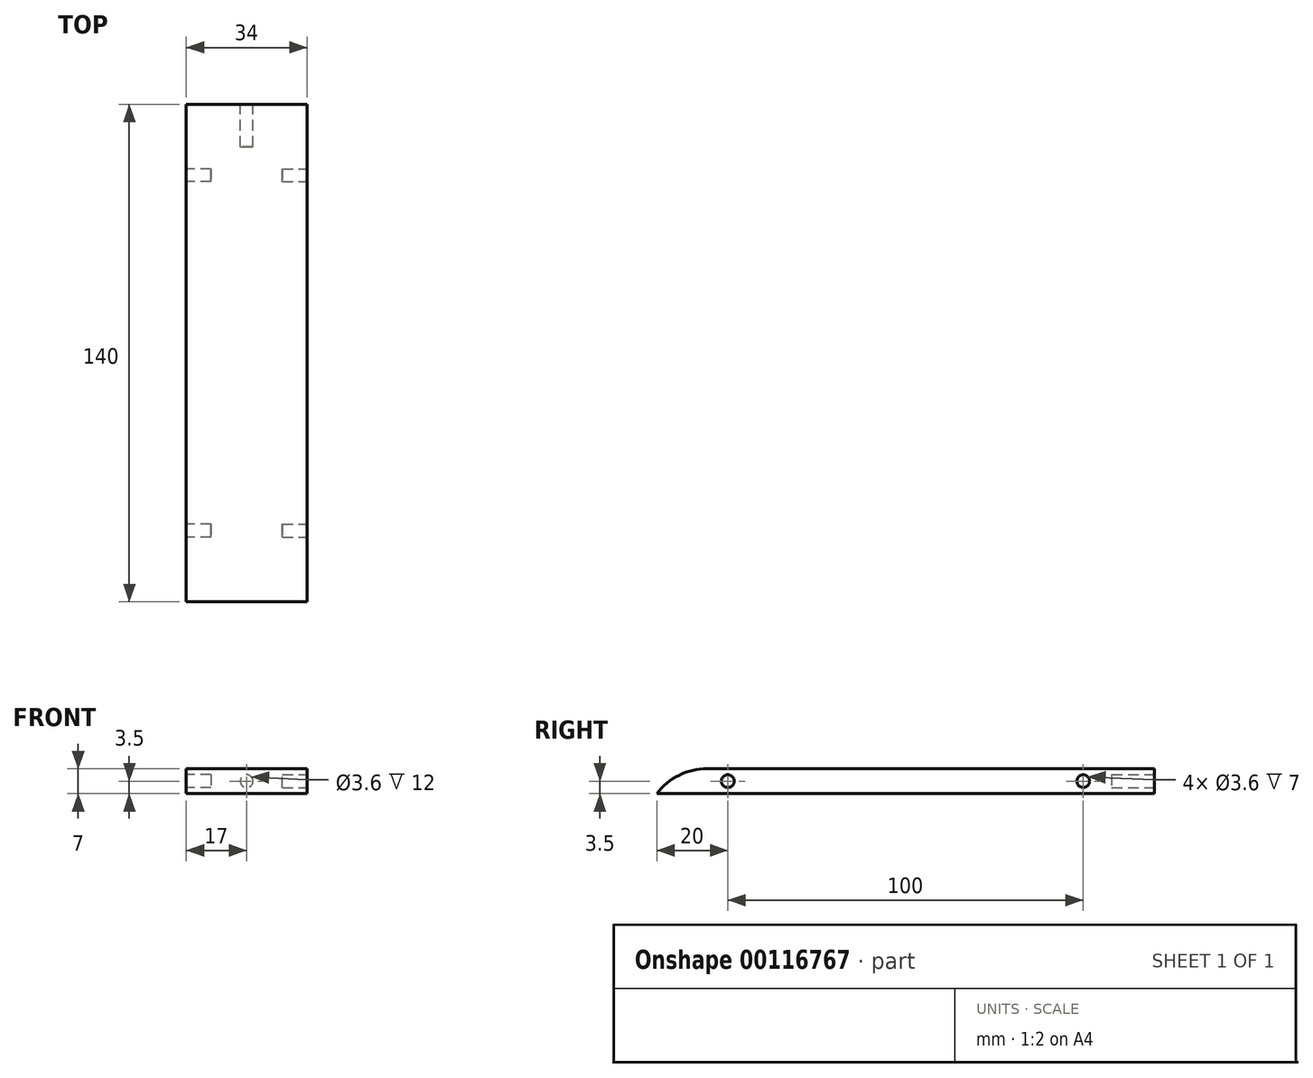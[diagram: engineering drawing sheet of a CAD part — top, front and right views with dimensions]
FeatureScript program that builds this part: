
annotation { "Feature Type Name" : "Feature", "Feature Type Description" : "" }
export const myFeature = defineFeature(function(context is Context, id is Id, definition is map)
    precondition{}
    {
        {
            var Q0;
            Q0=qCreatedBy(makeId("Right.planeOp"),FACE);
            var sketch = newSketch(context, id + "F0", { "sketchPlane" : qUnion([Q0])});
            skLineSegment(sketch, "E0", {"start": v(0, 0) * mm, "end": v(-140, 0) * mm});
            skLineSegment(sketch, "E1", {"start": v(-125.86, 7) * mm, "end": v(0, 7) * mm});
            skLineSegment(sketch, "E2", {"start": v(0, 7) * mm, "end": v(0, 0) * mm});
            skArc(sketch, "E3", {"start": v(-125.86, 7) * mm, "mid": v(-133.75, 5.15) * mm, "end": v(-140, 0) * mm});
            skSolve(sketch);
        }
        {
            var Q0;
            Q0=makeQuery(id+"F0.imprint","IMPRINT",FACE,{"disambiguationData":[TD([[makeQuery(id+"F0.imprint","IMPRINT",EDGE,{"derivedFrom":sQuery(id+"F0.wireOp",EDGE,"E0")}),-1.0]])]});
            extrude(context, id + "F1", {"entities" : qUnion([Q0]), "endBound" : BoundingType.SYMMETRIC, "depth" : 34 * mm});
        }
        {
            var Q0;
            Q0=makeQuery(id+"F1.opExtrude","CAP_FACE",FACE,{"disambiguationData":[OSD([sQuery(id+"F0.wireOp",EDGE,"E0"),sQuery(id+"F0.wireOp",EDGE,"E1"),sQuery(id+"F0.wireOp",EDGE,"E2"),sQuery(id+"F0.wireOp",EDGE,"E3")])],"isStart":false});
            var sketch = newSketch(context, id + "F2", { "sketchPlane" : qUnion([Q0])});
            skLineSegment(sketch, "E4", {"start": v(0, 0) * mm, "end": v(-20, 0) * mm, "construction": true});
            skLineSegment(sketch, "E5", {"start": v(-20, 0) * mm, "end": v(-20, 3.5) * mm, "construction": true});
            skLineSegment(sketch, "E6", {"start": v(-20, 3.5) * mm, "end": v(-120, 3.5) * mm, "construction": true});
            skCircle(sketch, "E7", {"center": v(-20, 3.5) * mm, "radius": 1.8 * mm});
            skCircle(sketch, "E8", {"center": v(-120, 3.5) * mm, "radius": 1.8 * mm});
            skSolve(sketch);
        }
        {
            var Q0;
            Q0 = qSketchRegion(id + "F2", true);
            extrude(context, id + "F3", {"entities" : qUnion([Q0]), "operationType" : NewBodyOperationType.REMOVE, "oppositeDirection" : true, "depth" : (15 - 8) * mm});
        }
        {
            var Q0;
            Q0=makeQuery(id+"F1.opExtrude","CAP_FACE",FACE,{"disambiguationData":[OSD([sQuery(id+"F0.wireOp",EDGE,"E0"),sQuery(id+"F0.wireOp",EDGE,"E1"),sQuery(id+"F0.wireOp",EDGE,"E2"),sQuery(id+"F0.wireOp",EDGE,"E3")])],"isStart":true});
            var sketch = newSketch(context, id + "F4", { "sketchPlane" : qUnion([Q0])});
            skLineSegment(sketch, "E9", {"start": v(0, 0) * mm, "end": v(20, 0) * mm, "construction": true});
            skLineSegment(sketch, "E10", {"start": v(20, 0) * mm, "end": v(20, 3.5) * mm, "construction": true});
            skLineSegment(sketch, "E11", {"start": v(20, 3.5) * mm, "end": v(120, 3.5) * mm, "construction": true});
            skCircle(sketch, "E12", {"center": v(20, 3.5) * mm, "radius": 1.8 * mm});
            skCircle(sketch, "E13", {"center": v(120, 3.5) * mm, "radius": 1.8 * mm});
            skSolve(sketch);
        }
        {
            var Q0;
            Q0 = qSketchRegion(id + "F4", true);
            extrude(context, id + "F5", {"entities" : qUnion([Q0]), "operationType" : NewBodyOperationType.REMOVE, "oppositeDirection" : true, "depth" : (15 - 8) * mm});
        }
        {
            var Q0;
            Q0=makeQuery(id+"F1.opExtrude","SWEPT_FACE",FACE,{"disambiguationData":[OSD([sQuery(id+"F0.wireOp",EDGE,"E2")])]});
            var sketch = newSketch(context, id + "F6", { "sketchPlane" : qUnion([Q0])});
            skLineSegment(sketch, "E14", {"start": v(0, 0) * mm, "end": v(0, 3.5) * mm, "construction": true});
            skCircle(sketch, "E15", {"center": v(0, 3.5) * mm, "radius": 1.8 * mm});
            skSolve(sketch);
        }
        {
            var Q0;
            Q0 = qSketchRegion(id + "F6", true);
            extrude(context, id + "F7", {"entities" : qUnion([Q0]), "operationType" : NewBodyOperationType.REMOVE, "oppositeDirection" : true, "depth" : 12 * mm});
        }
    });
